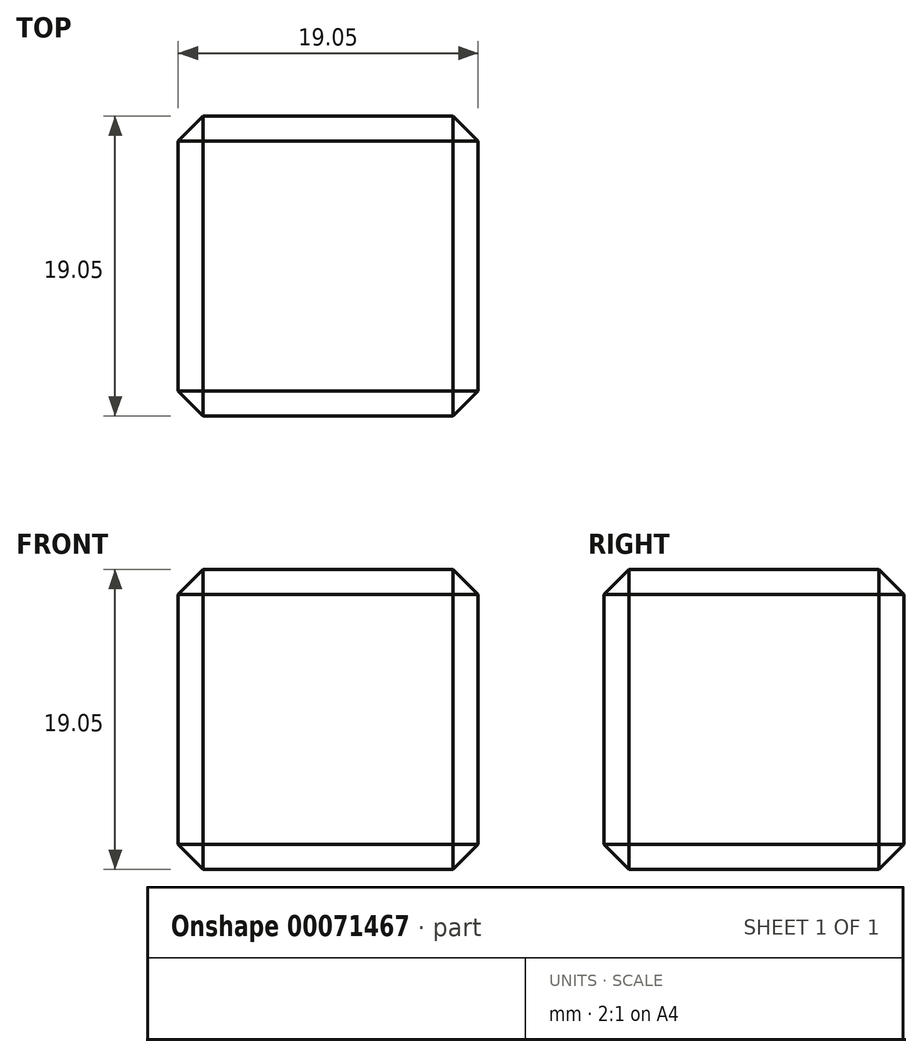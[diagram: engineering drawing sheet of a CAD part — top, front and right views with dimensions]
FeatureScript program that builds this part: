
annotation { "Feature Type Name" : "Feature", "Feature Type Description" : "" }
export const myFeature = defineFeature(function(context is Context, id is Id, definition is map)
    precondition{}
    {
        {
            var Q0;
            Q0=qCreatedBy(makeId("Top.planeOp"),FACE);
            var sketch = newSketch(context, id + "F0", { "sketchPlane" : qUnion([Q0])});
            skLineSegment(sketch, "E0.bottom", {"start": v(0, 0) * mm, "end": v(19.05, 0) * mm});
            skLineSegment(sketch, "E0.top", {"start": v(0, 19.05) * mm, "end": v(19.05, 19.05) * mm});
            skLineSegment(sketch, "E0.left", {"start": v(0, 0) * mm, "end": v(0, 19.05) * mm});
            skLineSegment(sketch, "E0.right", {"start": v(19.05, 0) * mm, "end": v(19.05, 19.05) * mm});
            skSolve(sketch);
        }
        {
            var Q0;
            Q0 = qSketchRegion(id + "F0", true);
            extrude(context, id + "F1", {"entities" : qUnion([Q0]), "depth" : 19.05 * mm});
        }
        {
            var Q0;
            Q0=makeQuery(id+"F1.opExtrude","SWEPT_FACE",FACE,{"disambiguationData":[OSD([sQuery(id+"F0.wireOp",EDGE,"E0.bottom")])]});
            var Q1;
            Q1=makeQuery(id+"F1.opExtrude","SWEPT_FACE",FACE,{"disambiguationData":[OSD([sQuery(id+"F0.wireOp",EDGE,"E0.right")])]});
            var Q2;
            Q2=makeQuery(id+"F1.opExtrude","CAP_FACE",FACE,{"disambiguationData":[OSD([sQuery(id+"F0.wireOp",EDGE,"E0.bottom"),sQuery(id+"F0.wireOp",EDGE,"E0.top"),sQuery(id+"F0.wireOp",EDGE,"E0.left"),sQuery(id+"F0.wireOp",EDGE,"E0.right")])],"isStart":false});
            var Q3;
            Q3=makeQuery(id+"F1.opExtrude","SWEPT_FACE",FACE,{"disambiguationData":[OSD([sQuery(id+"F0.wireOp",EDGE,"E0.top")])]});
            var Q4;
            Q4=makeQuery(id+"F1.opExtrude","CAP_FACE",FACE,{"disambiguationData":[OSD([sQuery(id+"F0.wireOp",EDGE,"E0.bottom"),sQuery(id+"F0.wireOp",EDGE,"E0.top"),sQuery(id+"F0.wireOp",EDGE,"E0.left"),sQuery(id+"F0.wireOp",EDGE,"E0.right")])],"isStart":true});
            var Q5;
            Q5=makeQuery(id+"F1.opExtrude","SWEPT_FACE",FACE,{"disambiguationData":[OSD([sQuery(id+"F0.wireOp",EDGE,"E0.left")])]});
            chamfer(context, id + "F2", {"entities" : qUnion([Q0, Q1, Q2, Q3, Q4, Q5]), "width" : 1.59 * mm, "tangentPropagation" : true});
        }
    });
